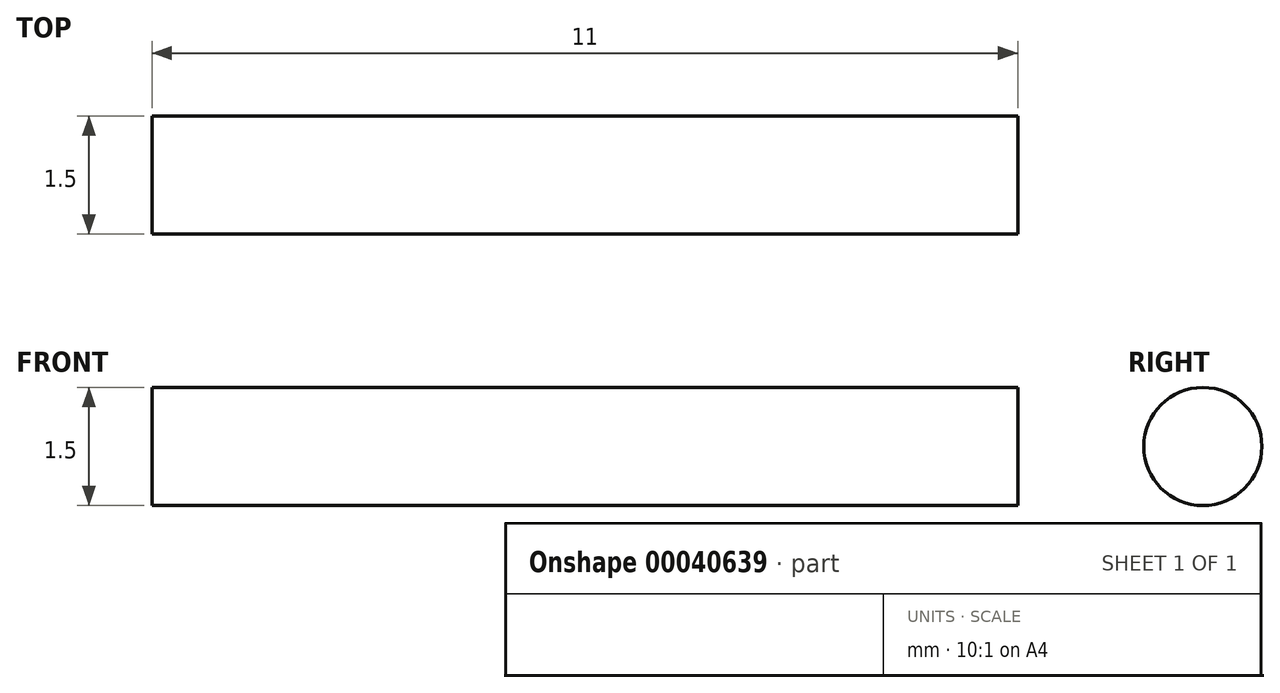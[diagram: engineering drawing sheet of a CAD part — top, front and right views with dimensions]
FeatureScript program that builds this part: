
annotation { "Feature Type Name" : "Feature", "Feature Type Description" : "" }
export const myFeature = defineFeature(function(context is Context, id is Id, definition is map)
    precondition{}
    {
        {
            var Q0;
            Q0=qCreatedBy(makeId("Top.planeOp"),FACE);
            var sketch = newSketch(context, id + "F0", { "sketchPlane" : qUnion([Q0])});
            skLineSegment(sketch, "E0", {"start": v(-50, 0) * mm, "end": v(50, 0) * mm, "construction": true});
            skLineSegment(sketch, "E1", {"start": v(0, 50) * mm, "end": v(0, -50) * mm, "construction": true});
            skSolve(sketch);
        }
        {
            var Q0;
            Q0=qCreatedBy(makeId("Front.planeOp"),FACE);
            var sketch = newSketch(context, id + "F1", { "sketchPlane" : qUnion([Q0])});
            skLineSegment(sketch, "E2.0", {"start": v(-50, 0) * mm, "end": v(50, 0) * mm, "construction": true});
            skLineSegment(sketch, "E3.bottom", {"start": v(-5.5, 0) * mm, "end": v(5.5, 0) * mm});
            skLineSegment(sketch, "E3.top", {"start": v(-5.5, 0.75) * mm, "end": v(5.5, 0.75) * mm});
            skLineSegment(sketch, "E3.left", {"start": v(-5.5, 0) * mm, "end": v(-5.5, 0.75) * mm});
            skLineSegment(sketch, "E3.right", {"start": v(5.5, 0) * mm, "end": v(5.5, 0.75) * mm});
            skSolve(sketch);
        }
        {
            var Q0;
            Q0=qSketchRegion(id+"F1",true);
            var Q1;
            Q1=sQuery(id+"F1.wireOp",EDGE,"E2.0");
            revolve(context, id + "F2", {"entities" : qUnion([Q0]), "axis" : qUnion([Q1]), "revolveType" : RevolveType.FULL});
        }
    });
